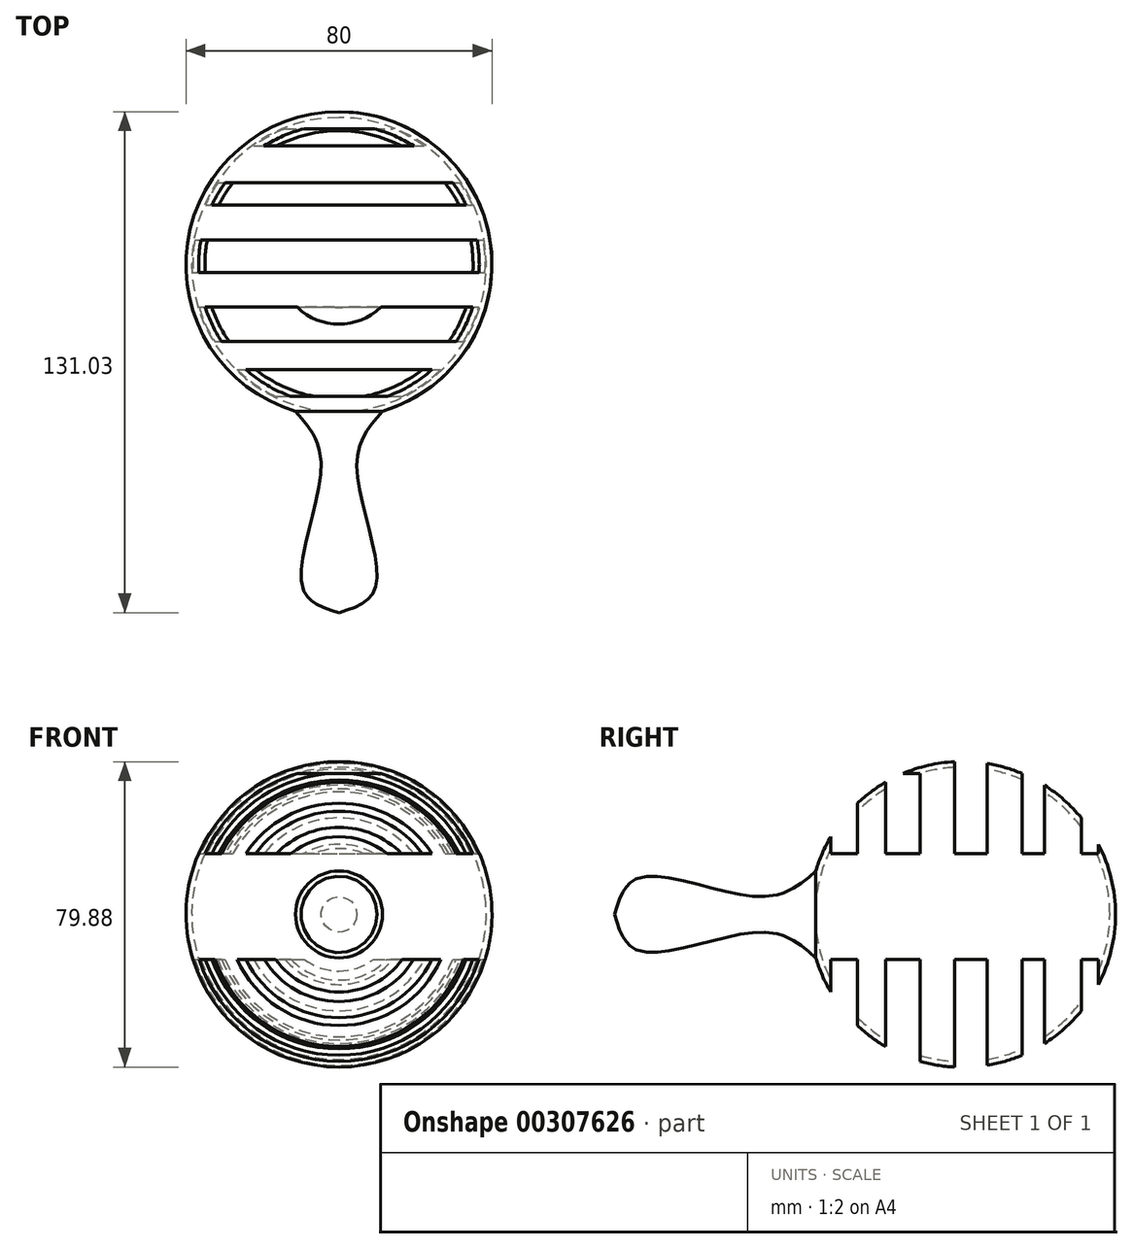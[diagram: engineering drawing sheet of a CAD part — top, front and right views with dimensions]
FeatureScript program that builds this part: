
annotation { "Feature Type Name" : "Feature", "Feature Type Description" : "" }
export const myFeature = defineFeature(function(context is Context, id is Id, definition is map)
    precondition{}
    {
        {
            var Q0;
            Q0=qCreatedBy(makeId("Top.planeOp"),FACE);
            var sketch = newSketch(context, id + "F0", { "sketchPlane" : qUnion([Q0])});
            skArc(sketch, "E0", {"start": v(11.37, -3.9) * mm, "mid": v(39.59, 40.2) * mm, "end": v(0, 74.46) * mm});
            skArc(sketch, "E1", {"start": v(0, -4.05) * mm, "mid": v(38.5, 34.46) * mm, "end": v(0, 72.96) * mm});
            skLineSegment(sketch, "E2", {"start": v(0, 74.46) * mm, "end": v(0, 34.46) * mm});
            skLineSegment(sketch, "E3.trimOffspring", {"start": v(0, -4.05) * mm, "end": v(0, -5.54) * mm});
            skLineSegment(sketch, "E4", {"start": v(11.37, -5.54) * mm, "end": v(11.37, -3.9) * mm, "construction": true});
            skFitSpline(sketch, "E5", {"points": [v(11.37, -3.9) * mm, v(4.65, -18.07) * mm, v(9.68, -49.65) * mm, v(0, -56.57) * mm], "startDerivative": vector(-33.19, -37.54) * mm, "endDerivative": vector(-48.8, -14.83) * mm});
            skLineSegment(sketch, "E6", {"start": v(0, -56.57) * mm, "end": v(0, -4.05) * mm});
            skSolve(sketch);
        }
        {
            var Q0;
            {var subQ2=sQuery(id+"F0.wireOp",EDGE,"E0");Q0=makeQuery(id+"F0.imprint","IMPRINT",FACE,{"disambiguationData":[TD([[makeQuery(id+"F0.imprint","IMPRINT",EDGE,{"derivedFrom":subQ2}),1.0]])]});}
            var Q1;
            Q1=sQuery(id+"F0.wireOp",EDGE,"E6");
            revolve(context, id + "F1", {"entities" : qUnion([Q0]), "axis" : qUnion([Q1]), "revolveType" : RevolveType.FULL});
        }
        {
            var Q0;
            Q0=qCreatedBy(makeId("Right.planeOp"),FACE);
            var sketch = newSketch(context, id + "F2", { "sketchPlane" : qUnion([Q0])});
            skLineSegment(sketch, "E7.bottom", {"start": v(0, 15.93) * mm, "end": v(7, 15.93) * mm});
            skLineSegment(sketch, "E7.top", {"start": v(0, -11.74) * mm, "end": v(7, -11.74) * mm});
            skLineSegment(sketch, "E8.left", {"start": v(81.9, -11.74) * mm, "end": v(81.9, -11.74) * mm});
            skLineSegment(sketch, "E8.right", {"start": v(76.43, -11.74) * mm, "end": v(76.43, -11.74) * mm});
            skLineSegment(sketch, "E9.bottom", {"start": v(14.33, 36.84) * mm, "end": v(23.34, 36.84) * mm});
            skLineSegment(sketch, "E9.top", {"start": v(14.33, -43.92) * mm, "end": v(23.34, -43.92) * mm});
            skLineSegment(sketch, "E9.left", {"start": v(14.33, 36.84) * mm, "end": v(14.33, 15.93) * mm});
            skLineSegment(sketch, "E9.right", {"start": v(23.34, 36.84) * mm, "end": v(23.34, 15.93) * mm});
            skPoint(sketch, "E10.oppositeSnap0", {"position": v(40.95, -11.74) * mm});
            skLineSegment(sketch, "E10.bottom", {"start": v(32.35, 44.57) * mm, "end": v(40.95, 44.57) * mm});
            skLineSegment(sketch, "E10.top", {"start": v(32.35, -44.57) * mm, "end": v(40.95, -44.57) * mm});
            skLineSegment(sketch, "E10.left", {"start": v(32.35, 44.57) * mm, "end": v(32.35, 15.93) * mm});
            skLineSegment(sketch, "E10.right", {"start": v(40.95, 44.57) * mm, "end": v(40.95, 15.93) * mm});
            skLineSegment(sketch, "E11.bottom", {"start": v(50.04, 43.28) * mm, "end": v(55.84, 43.28) * mm});
            skLineSegment(sketch, "E11.top", {"start": v(50.04, -44.24) * mm, "end": v(55.84, -44.24) * mm});
            skLineSegment(sketch, "E11.left", {"start": v(50.04, 43.28) * mm, "end": v(50.04, 15.93) * mm});
            skLineSegment(sketch, "E11.right", {"start": v(55.84, 43.28) * mm, "end": v(55.84, 15.93) * mm});
            skLineSegment(sketch, "E12.bottom", {"start": v(65.49, 34.27) * mm, "end": v(70, 34.27) * mm});
            skLineSegment(sketch, "E12.top", {"start": v(65.49, -32.98) * mm, "end": v(70, -32.98) * mm});
            skLineSegment(sketch, "E12.left", {"start": v(65.49, 34.27) * mm, "end": v(65.49, 15.93) * mm});
            skLineSegment(sketch, "E12.right", {"start": v(70, 34.27) * mm, "end": v(70, 15.93) * mm});
            skLineSegment(sketch, "E13.bottom", {"start": v(0, 29.6) * mm, "end": v(7, 29.6) * mm});
            skLineSegment(sketch, "E13.top", {"start": v(0, -30.4) * mm, "end": v(7, -30.4) * mm});
            skLineSegment(sketch, "E13.left", {"start": v(0, 29.6) * mm, "end": v(0, 15.93) * mm});
            skLineSegment(sketch, "E13.right", {"start": v(7, 29.6) * mm, "end": v(7, 15.93) * mm});
            skLineSegment(sketch, "E14.trimOffspring", {"start": v(14.33, 15.93) * mm, "end": v(23.34, 15.93) * mm});
            skLineSegment(sketch, "E15.trimOffspring", {"start": v(32.35, 15.93) * mm, "end": v(40.95, 15.93) * mm});
            skLineSegment(sketch, "E16.trimOffspring", {"start": v(50.04, 15.93) * mm, "end": v(55.84, 15.93) * mm});
            skLineSegment(sketch, "E17.trimOffspring", {"start": v(65.49, 15.93) * mm, "end": v(70, 15.93) * mm});
            skLineSegment(sketch, "E18.trimOffspring", {"start": v(65.49, -11.74) * mm, "end": v(70, -11.74) * mm});
            skLineSegment(sketch, "E19.trimOffspring", {"start": v(50.04, -11.74) * mm, "end": v(55.84, -11.74) * mm});
            skLineSegment(sketch, "E20.trimOffspring", {"start": v(32.35, -11.74) * mm, "end": v(40.95, -11.74) * mm});
            skLineSegment(sketch, "E21.trimOffspring", {"start": v(14.33, -11.74) * mm, "end": v(23.34, -11.74) * mm});
            skLineSegment(sketch, "E22.trimOffspring", {"start": v(65.49, -11.74) * mm, "end": v(65.49, -32.98) * mm});
            skLineSegment(sketch, "E23.trimOffspring", {"start": v(70, -11.74) * mm, "end": v(70, -32.98) * mm});
            skLineSegment(sketch, "E24.trimOffspring", {"start": v(55.84, -11.74) * mm, "end": v(55.84, -44.24) * mm});
            skLineSegment(sketch, "E25.trimOffspring", {"start": v(50.04, -11.74) * mm, "end": v(50.04, -44.24) * mm});
            skLineSegment(sketch, "E26.trimOffspring", {"start": v(40.95, -11.74) * mm, "end": v(40.95, -44.57) * mm});
            skLineSegment(sketch, "E27.trimOffspring", {"start": v(32.35, -11.74) * mm, "end": v(32.35, -44.57) * mm});
            skLineSegment(sketch, "E28.trimOffspring", {"start": v(23.34, -11.74) * mm, "end": v(23.34, -43.92) * mm});
            skLineSegment(sketch, "E29.trimOffspring", {"start": v(14.33, -11.74) * mm, "end": v(14.33, -43.92) * mm});
            skLineSegment(sketch, "E30.trimOffspring", {"start": v(7, -11.74) * mm, "end": v(7, -30.4) * mm});
            skLineSegment(sketch, "E31.trimOffspring", {"start": v(0, -11.74) * mm, "end": v(0, -30.4) * mm});
            skSolve(sketch);
        }
        {
            var Q0;
            Q0=makeQuery(id+"F2.imprint","IMPRINT",FACE,{"disambiguationData":[TD([[makeQuery(id+"F2.imprint","IMPRINT",EDGE,{"derivedFrom":sQuery(id+"F2.wireOp",EDGE,"E7.bottom")}),1.0]])]});
            var Q1;
            Q1=makeQuery(id+"F2.imprint","IMPRINT",FACE,{"disambiguationData":[TD([[makeQuery(id+"F2.imprint","IMPRINT",EDGE,{"derivedFrom":sQuery(id+"F2.wireOp",EDGE,"E9.bottom")}),-1.0]])]});
            var Q2;
            Q2=makeQuery(id+"F2.imprint","IMPRINT",FACE,{"disambiguationData":[TD([[makeQuery(id+"F2.imprint","IMPRINT",EDGE,{"derivedFrom":sQuery(id+"F2.wireOp",EDGE,"E10.bottom")}),-1.0]])]});
            var Q3;
            Q3=makeQuery(id+"F2.imprint","IMPRINT",FACE,{"disambiguationData":[TD([[makeQuery(id+"F2.imprint","IMPRINT",EDGE,{"derivedFrom":sQuery(id+"F2.wireOp",EDGE,"E11.bottom")}),-1.0]])]});
            var Q4;
            Q4=makeQuery(id+"F2.imprint","IMPRINT",FACE,{"disambiguationData":[TD([[makeQuery(id+"F2.imprint","IMPRINT",EDGE,{"derivedFrom":sQuery(id+"F2.wireOp",EDGE,"E12.bottom")}),-1.0]])]});
            var Q5;
            Q5=makeQuery(id+"F2.imprint","IMPRINT",FACE,{"disambiguationData":[TD([[makeQuery(id+"F2.imprint","IMPRINT",EDGE,{"derivedFrom":sQuery(id+"F2.wireOp",EDGE,"E7.top")}),-1.0]])]});
            var Q6;
            Q6=makeQuery(id+"F2.imprint","IMPRINT",FACE,{"disambiguationData":[TD([[makeQuery(id+"F2.imprint","IMPRINT",EDGE,{"derivedFrom":sQuery(id+"F2.wireOp",EDGE,"E9.top")}),1.0]])]});
            var Q7;
            Q7=makeQuery(id+"F2.imprint","IMPRINT",FACE,{"disambiguationData":[TD([[makeQuery(id+"F2.imprint","IMPRINT",EDGE,{"derivedFrom":sQuery(id+"F2.wireOp",EDGE,"E10.top")}),1.0]])]});
            var Q8;
            Q8=makeQuery(id+"F2.imprint","IMPRINT",FACE,{"disambiguationData":[TD([[makeQuery(id+"F2.imprint","IMPRINT",EDGE,{"derivedFrom":sQuery(id+"F2.wireOp",EDGE,"E11.top")}),1.0]])]});
            var Q9;
            Q9=makeQuery(id+"F2.imprint","IMPRINT",FACE,{"disambiguationData":[TD([[makeQuery(id+"F2.imprint","IMPRINT",EDGE,{"derivedFrom":sQuery(id+"F2.wireOp",EDGE,"E12.top")}),1.0]])]});
            extrude(context, id + "F3", {"entities" : qUnion([Q0, Q1, Q2, Q3, Q4, Q5, Q6, Q7, Q8, Q9]), "operationType" : NewBodyOperationType.REMOVE, "endBound" : BoundingType.SYMMETRIC, "oppositeDirection" : true, "depth" : 80 * mm});
        }
    });
